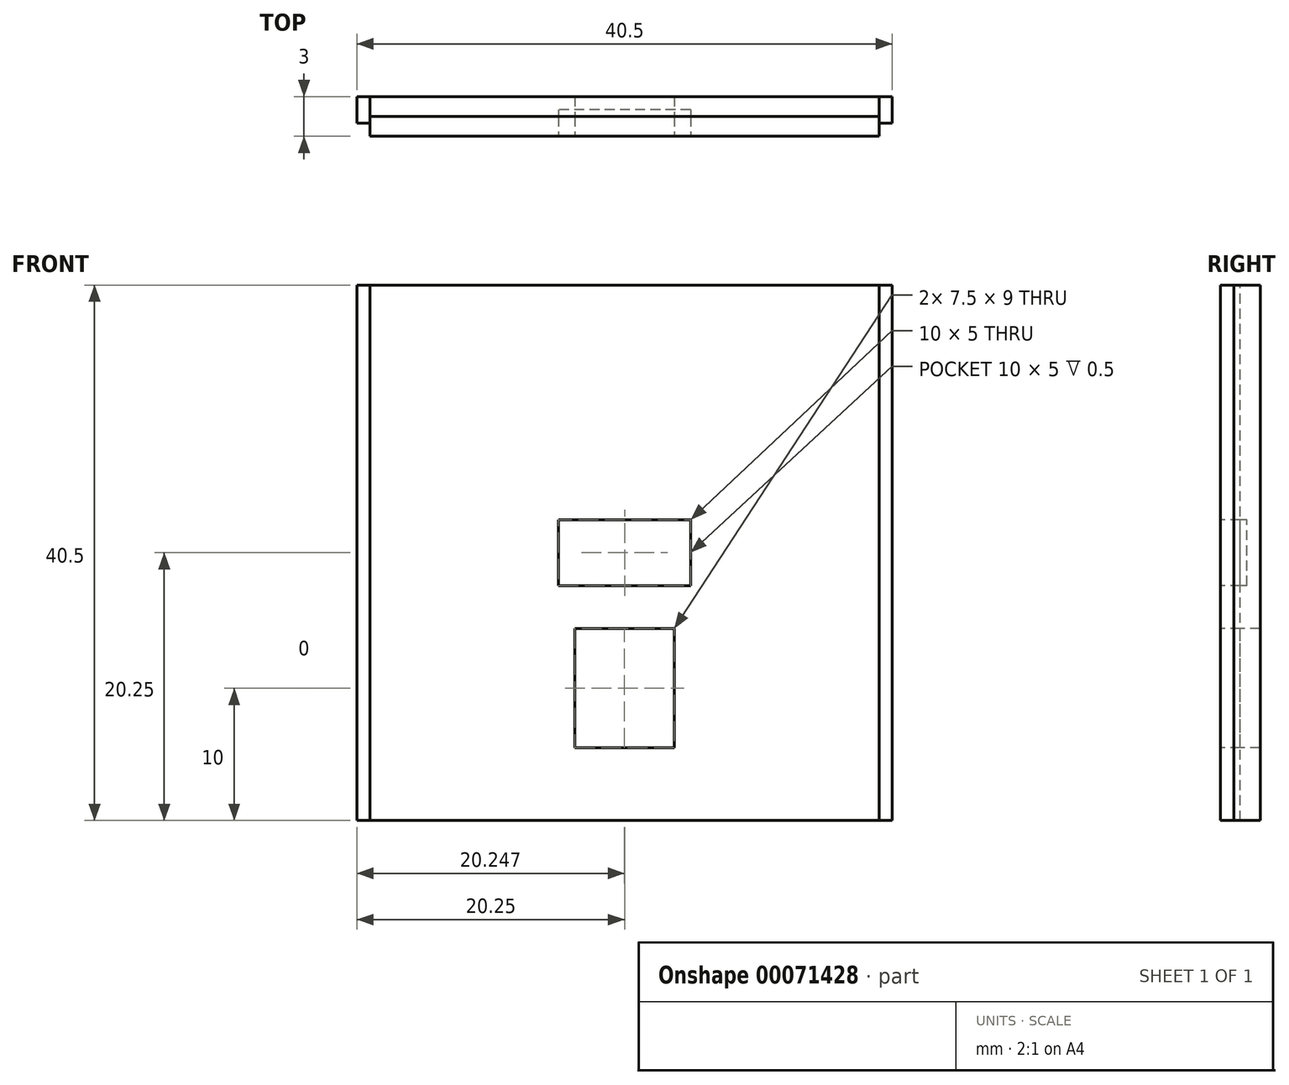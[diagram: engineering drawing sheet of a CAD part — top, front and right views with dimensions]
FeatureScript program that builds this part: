
annotation { "Feature Type Name" : "Feature", "Feature Type Description" : "" }
export const myFeature = defineFeature(function(context is Context, id is Id, definition is map)
    precondition{}
    {
        {
            var Q0;
            Q0=qCreatedBy(makeId("Front.planeOp"),FACE);
            var sketch = newSketch(context, id + "F0", { "sketchPlane" : qUnion([Q0])});
            skLineSegment(sketch, "E0.rect.bottom", {"start": v(-19.25, -20.25) * mm, "end": v(19.25, -20.25) * mm});
            skLineSegment(sketch, "E0.rect.top", {"start": v(-19.25, 20.25) * mm, "end": v(19.25, 20.25) * mm});
            skLineSegment(sketch, "E0.rect.left", {"start": v(-19.25, -20.25) * mm, "end": v(-19.25, 20.25) * mm});
            skLineSegment(sketch, "E0.rect.right", {"start": v(19.25, -20.25) * mm, "end": v(19.25, 20.25) * mm});
            skPoint(sketch, "E0.rect.middle", {"position": v(0, 0) * mm});
            skSolve(sketch);
        }
        {
            var Q0;
            Q0=sQuery(id+"F0.wireOp",EDGE,"E0.rect.top");
            cPlane(context, id + "F1", {"entities" : qUnion([Q0]), "cplaneType" : CPlaneType.LINE_ANGLE, "offset" : 0 * mm, "angle" : 90 * degree, "width" : 152.4 * mm, "height" : 152.4 * mm});
        }
        {
            var Q0;
            Q0=qCreatedBy(id+"F1.planeOp",FACE);
            var sketch = newSketch(context, id + "F2", { "sketchPlane" : qUnion([Q0])});
            skLineSegment(sketch, "E1.rect.bottom", {"start": v(19.25, -0.5) * mm, "end": v(20.25, -0.5) * mm});
            skLineSegment(sketch, "E1.rect.top", {"start": v(19.25, 1.5) * mm, "end": v(20.25, 1.5) * mm});
            skLineSegment(sketch, "E1.rect.left", {"start": v(19.25, -0.5) * mm, "end": v(19.25, 1.5) * mm});
            skLineSegment(sketch, "E1.rect.right", {"start": v(20.25, -0.5) * mm, "end": v(20.25, 1.5) * mm});
            skLineSegment(sketch, "E2.MirrorCS", {"start": v(-19.25, -0.5) * mm, "end": v(-20.25, -0.5) * mm});
            skLineSegment(sketch, "E3.MirrorCS", {"start": v(-20.25, -0.5) * mm, "end": v(-20.25, 1.5) * mm});
            skPoint(sketch, "E4.MirrorP", {"position": v(-19.75, 0) * mm});
            skLineSegment(sketch, "E5.MirrorCS", {"start": v(-19.25, 1.5) * mm, "end": v(-20.25, 1.5) * mm});
            skLineSegment(sketch, "E6.MirrorCS", {"start": v(-19.25, -0.5) * mm, "end": v(-19.25, 1.5) * mm});
            skSolve(sketch);
        }
        {
            var Q0;
            Q0=makeQuery(id+"F2.imprint","IMPRINT",FACE,{"disambiguationData":[TD([[makeQuery(id+"F2.imprint","IMPRINT",EDGE,{"derivedFrom":sQuery(id+"F2.wireOp",EDGE,"E3.MirrorCS")}),-1.0]])]});
            var Q1;
            Q1=makeQuery(id+"F2.imprint","IMPRINT",FACE,{"disambiguationData":[TD([[makeQuery(id+"F2.imprint","IMPRINT",EDGE,{"derivedFrom":sQuery(id+"F2.wireOp",EDGE,"E1.rect.bottom")}),1.0]])]});
            extrude(context, id + "F3", {"entities" : qUnion([Q0, Q1]), "oppositeDirection" : true, "depth" : 40.5 * mm});
        }
        {
            var Q0;
            Q0=makeQuery(id+"F0.imprint","IMPRINT",FACE,{"disambiguationData":[TD([[makeQuery(id+"F0.imprint","IMPRINT",EDGE,{"derivedFrom":sQuery(id+"F0.wireOp",EDGE,"E0.rect.bottom")}),1.0]])]});
            extrude(context, id + "F4", {"entities" : qUnion([Q0]), "oppositeDirection" : true, "depth" : 1.5 * mm});
        }
        {
            var Q0;
            Q0=makeQuery(id+"F4.opExtrude","CAP_FACE",FACE,{"disambiguationData":[OSD([sQuery(id+"F0.wireOp",EDGE,"E0.rect.bottom"),sQuery(id+"F0.wireOp",EDGE,"E0.rect.top"),sQuery(id+"F0.wireOp",EDGE,"E0.rect.left"),sQuery(id+"F0.wireOp",EDGE,"E0.rect.right")])],"isStart":true});
            extrude(context, id + "F5", {"entities" : qUnion([Q0]), "depth" : 1.5 * mm});
        }
        {
            var Q0;
            Q0=makeQuery(id+"F5.opExtrude","CAP_FACE",FACE,{"disambiguationData":[OSD([sQuery(id+"F0.wireOp",EDGE,"E0.rect.bottom"),sQuery(id+"F0.wireOp",EDGE,"E0.rect.top"),sQuery(id+"F0.wireOp",EDGE,"E0.rect.left"),sQuery(id+"F0.wireOp",EDGE,"E0.rect.right")])],"isStart":false});
            cPlane(context, id + "F6", {"entities" : qUnion([Q0]), "cplaneType" : CPlaneType.OFFSET, "offset" : 0 * mm, "width" : 152.4 * mm, "height" : 152.4 * mm});
        }
        {
            var Q0;
            Q0=qCreatedBy(id+"F6.planeOp",FACE);
            var sketch = newSketch(context, id + "F7", { "sketchPlane" : qUnion([Q0])});
            skLineSegment(sketch, "E7.rect.bottom", {"start": v(5, -2.5) * mm, "end": v(-5, -2.5) * mm});
            skLineSegment(sketch, "E7.rect.top", {"start": v(5, 2.5) * mm, "end": v(-5, 2.5) * mm});
            skLineSegment(sketch, "E7.rect.left", {"start": v(5, -2.5) * mm, "end": v(5, 2.5) * mm});
            skLineSegment(sketch, "E7.rect.right", {"start": v(-5, -2.5) * mm, "end": v(-5, 2.5) * mm});
            skPoint(sketch, "E7.rect.middle", {"position": v(0, 0) * mm});
            skSolve(sketch);
        }
        {
            var Q0;
            Q0=makeQuery(id+"F7.imprint","IMPRINT",FACE,{"disambiguationData":[TD([[makeQuery(id+"F7.imprint","IMPRINT",EDGE,{"derivedFrom":sQuery(id+"F7.wireOp",EDGE,"E7.rect.bottom")}),-1.0]])]});
            extrude(context, id + "F8", {"entities" : qUnion([Q0]), "operationType" : NewBodyOperationType.REMOVE, "oppositeDirection" : true, "depth" : 2 * mm});
        }
        {
            var Q0;
            Q0=qCreatedBy(id+"F6.planeOp",FACE);
            var sketch = newSketch(context, id + "F9", { "sketchPlane" : qUnion([Q0])});
            skLineSegment(sketch, "E8.rect.bottom", {"start": v(-3.75, -14.75) * mm, "end": v(3.75, -14.75) * mm});
            skLineSegment(sketch, "E8.rect.top", {"start": v(-3.75, -5.75) * mm, "end": v(3.75, -5.75) * mm});
            skLineSegment(sketch, "E8.rect.left", {"start": v(-3.75, -14.75) * mm, "end": v(-3.75, -5.75) * mm});
            skLineSegment(sketch, "E8.rect.right", {"start": v(3.75, -14.75) * mm, "end": v(3.75, -5.75) * mm});
            skPoint(sketch, "E8.rect.middle", {"position": v(0, -10.25) * mm});
            skSolve(sketch);
        }
        {
            var Q0;
            Q0=makeQuery(id+"F9.imprint","IMPRINT",FACE,{"disambiguationData":[TD([[makeQuery(id+"F9.imprint","IMPRINT",EDGE,{"derivedFrom":sQuery(id+"F9.wireOp",EDGE,"E8.rect.bottom")}),1.0]])]});
            extrude(context, id + "F10", {"entities" : qUnion([Q0]), "operationType" : NewBodyOperationType.REMOVE, "oppositeDirection" : true, "depth" : 76.2 * mm});
        }
        {
            var Q0;
            Q0=makeQuery(id+"F4.opExtrude","CAP_FACE",FACE,{"disambiguationData":[OSD([sQuery(id+"F0.wireOp",EDGE,"E0.rect.bottom"),sQuery(id+"F0.wireOp",EDGE,"E0.rect.top"),sQuery(id+"F0.wireOp",EDGE,"E0.rect.left"),sQuery(id+"F0.wireOp",EDGE,"E0.rect.right")])],"isStart":false});
            cPlane(context, id + "F11", {"entities" : qUnion([Q0]), "cplaneType" : CPlaneType.OFFSET, "offset" : 0 * mm, "width" : 152.4 * mm, "height" : 152.4 * mm});
        }
        {
            var Q0;
            Q0=qCreatedBy(id+"F11.planeOp",FACE);
            var sketch = newSketch(context, id + "F12", { "sketchPlane" : qUnion([Q0])});
            skLineSegment(sketch, "E9.rect.bottom", {"start": v(-3.75, -14.75) * mm, "end": v(3.75, -14.75) * mm});
            skLineSegment(sketch, "E9.rect.top", {"start": v(-3.75, -5.75) * mm, "end": v(3.75, -5.75) * mm});
            skLineSegment(sketch, "E9.rect.left", {"start": v(-3.75, -14.75) * mm, "end": v(-3.75, -5.75) * mm});
            skLineSegment(sketch, "E9.rect.right", {"start": v(3.75, -14.75) * mm, "end": v(3.75, -5.75) * mm});
            skPoint(sketch, "E9.rect.middle", {"position": v(0, -10.25) * mm});
            skSolve(sketch);
        }
        {
            var Q0;
            Q0=makeQuery(id+"F12.imprint","IMPRINT",FACE,{"disambiguationData":[TD([[makeQuery(id+"F12.imprint","IMPRINT",EDGE,{"derivedFrom":sQuery(id+"F12.wireOp",EDGE,"E9.rect.bottom")}),1.0]])]});
            extrude(context, id + "F13", {"entities" : qUnion([Q0]), "operationType" : NewBodyOperationType.REMOVE, "oppositeDirection" : true, "depth" : 3 * mm});
        }
    });
